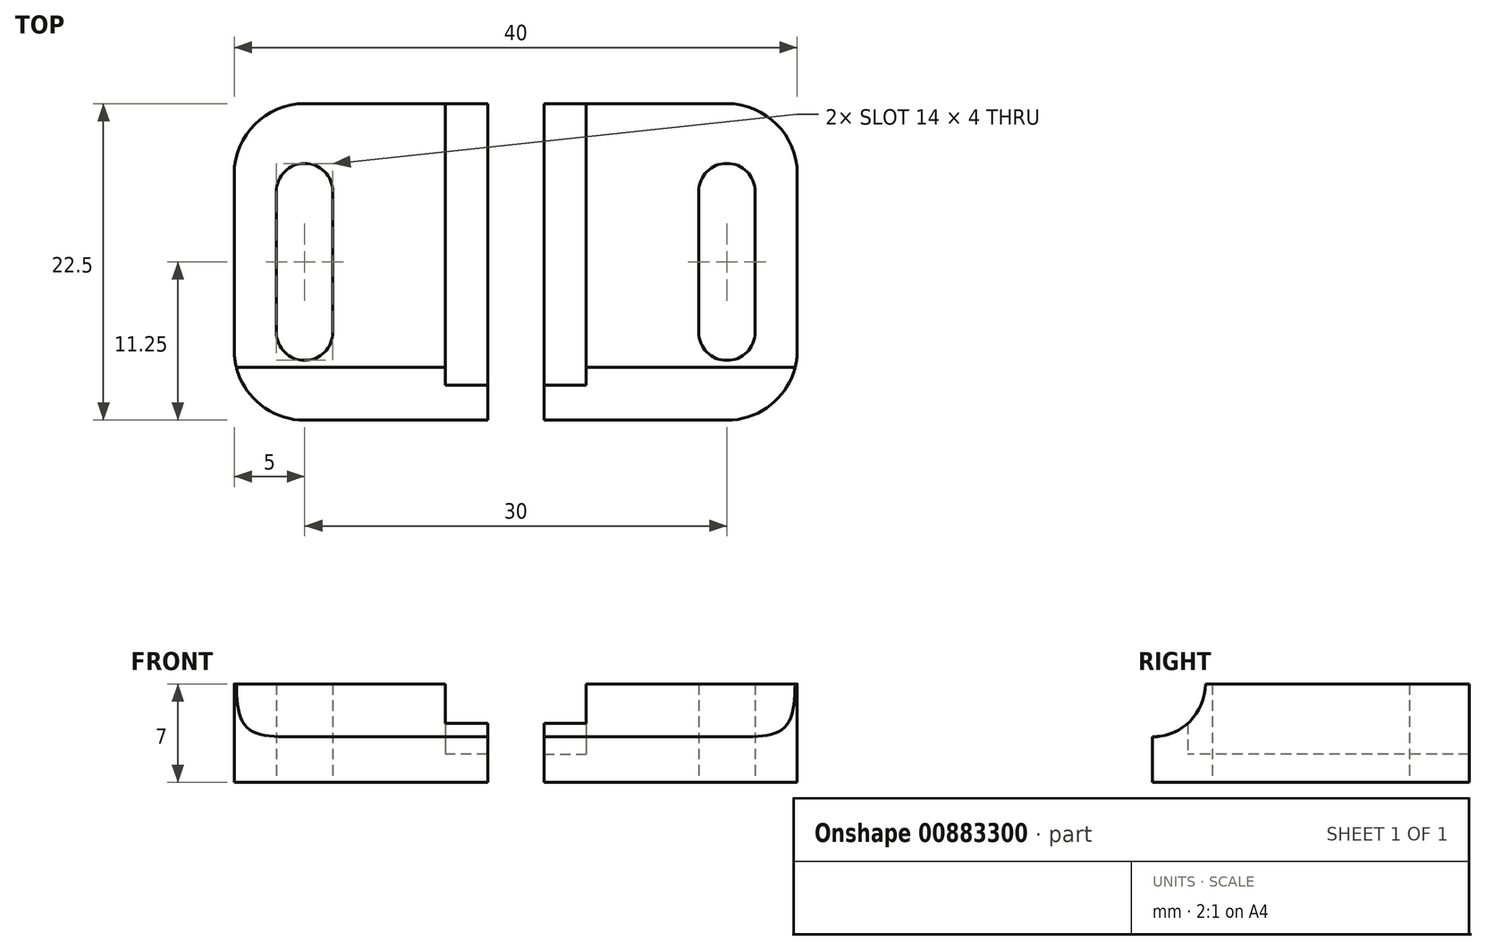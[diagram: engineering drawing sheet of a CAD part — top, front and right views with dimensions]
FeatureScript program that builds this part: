
annotation { "Feature Type Name" : "Feature", "Feature Type Description" : "" }
export const myFeature = defineFeature(function(context is Context, id is Id, definition is map)
    precondition{}
    {
        {
            var Q0;
            Q0=qCreatedBy(makeId("Top.planeOp"),FACE);
            var sketch = newSketch(context, id + "F0", { "sketchPlane" : qUnion([Q0])});
            skLineSegment(sketch, "E0", {"start": v(-2, 0) * mm, "end": v(-2, 2.5) * mm});
            skLineSegment(sketch, "E1", {"start": v(0, 2.5) * mm, "end": v(-5, 2.5) * mm});
            skLineSegment(sketch, "E2", {"start": v(-5, 2.5) * mm, "end": v(-5, 22.5) * mm});
            skLineSegment(sketch, "E3", {"start": v(-5, 22.5) * mm, "end": v(-20, 22.5) * mm});
            skLineSegment(sketch, "E4", {"start": v(-20, 22.5) * mm, "end": v(-20, 0) * mm});
            skLineSegment(sketch, "E5", {"start": v(-20, 0) * mm, "end": v(0, 0) * mm});
            skLineSegment(sketch, "E6", {"start": v(-20, 22.5) * mm, "end": v(-15, 22.5) * mm});
            skLineSegment(sketch, "E7.left", {"start": v(-13, 16.25) * mm, "end": v(-13, 6.25) * mm});
            skLineSegment(sketch, "E7.right", {"start": v(-17, 16.25) * mm, "end": v(-17, 6.25) * mm});
            skPoint(sketch, "E7.middle", {"position": v(-15, 11.25) * mm});
            skCircle(sketch, "E8", {"center": v(-15, 16.25) * mm, "radius": 2 * mm});
            skCircle(sketch, "E9", {"center": v(-15, 6.25) * mm, "radius": 2 * mm});
            skLineSegment(sketch, "E10", {"start": v(-5, 22.5) * mm, "end": v(0, 22.5) * mm});
            skLineSegment(sketch, "E11", {"start": v(-2, 22.5) * mm, "end": v(-2, 2.5) * mm});
            skSolve(sketch);
        }
        {
            var Q0;
            Q0=makeQuery(id+"F0.imprint","IMPRINT",FACE,{"disambiguationData":[TD([[makeQuery(id+"F0.imprint","IMPRINT",EDGE,{"derivedFrom":sQuery(id+"F0.wireOp",EDGE,"E0")}),1.0]])]});
            extrude(context, id + "F1", {"entities" : qUnion([Q0]), "depth" : 5 * mm, "offsetDistance" : 25 * mm});
        }
        {
            var Q0;
            Q0 = qSketchRegion(id + "F0", true);
            extrude(context, id + "F2", {"entities" : qUnion([Q0]), "operationType" : NewBodyOperationType.ADD, "depth" : -2 * mm, "offsetDistance" : 25 * mm});
        }
        {
            var Q0;
            {var subQ0=sQuery(id+"F0.wireOp",EDGE,"E0");Q0=makeQuery(id+"F2.boolean.opBoolean","MERGE",FACE,{"derivedFrom":[makeQuery(id+"F1.opExtrude","SWEPT_FACE",FACE,{"disambiguationData":[OSD([subQ0])]}),makeQuery(id+"F2.opExtrude","SWEPT_FACE",FACE,{"disambiguationData":[OSD([subQ0,sQuery(id+"F0.wireOp",EDGE,"E11")])]})]});}
            var sketch = newSketch(context, id + "F3", { "sketchPlane" : qUnion([Q0])});
            skCircle(sketch, "E12", {"center": v(0, 5) * mm, "radius": 3.75 * mm});
            skSolve(sketch);
        }
        {
            var Q0;
            Q0 = qSketchRegion(id + "F3", true);
            extrude(context, id + "F4", {"entities" : qUnion([Q0]), "operationType" : NewBodyOperationType.REMOVE, "oppositeDirection" : true, "depth" : 25 * mm, "offsetDistance" : 25 * mm});
        }
        {
            var Q0;
            {var subQ0=sQuery(id+"F0.wireOp",EDGE,"E5");var subQ1=sQuery(id+"F0.wireOp",EDGE,"E4");Q0=makeQuery(id+"F2.boolean.opBoolean","MERGE",EDGE,{"derivedFrom":[makeQuery(id+"F1.opExtrude","SWEPT_EDGE",EDGE,{"disambiguationData":[OSD([subQ1,subQ0])]}),makeQuery(id+"F2.opExtrude","SWEPT_EDGE",EDGE,{"disambiguationData":[OSD([subQ1,subQ0])]})]});}
            var Q1;
            {var subQ0=sQuery(id+"F0.wireOp",EDGE,"E4");var subQ1=sQuery(id+"F0.wireOp",EDGE,"E3");Q1=makeQuery(id+"F2.boolean.opBoolean","MERGE",EDGE,{"derivedFrom":[makeQuery(id+"F1.opExtrude","SWEPT_EDGE",EDGE,{"disambiguationData":[OSD([subQ1,subQ0])]}),makeQuery(id+"F2.opExtrude","SWEPT_EDGE",EDGE,{"disambiguationData":[OSD([subQ1,subQ0])]})]});}
            fillet(context, id + "F5", {"entities" : qUnion([Q0, Q1]), "tangentPropagation" : true, "radius" : 5 * mm, "defaultsChanged" : false, "vertexSettings" : [], "allowEdgeOverflow" : false});
        }
        {
            var Q0;
            Q0=makeQuery(id+"F1.opExtrude","SWEPT_BODY",BODY,{"disambiguationData":[OSD([sQuery(id+"F0.wireOp",EDGE,"E0"),sQuery(id+"F0.wireOp",EDGE,"E1"),sQuery(id+"F0.wireOp",EDGE,"E2"),sQuery(id+"F0.wireOp",EDGE,"E3"),sQuery(id+"F0.wireOp",EDGE,"E4"),sQuery(id+"F0.wireOp",EDGE,"E5"),sQuery(id+"F0.wireOp",EDGE,"E7.left"),sQuery(id+"F0.wireOp",EDGE,"E7.right"),sQuery(id+"F0.wireOp",EDGE,"E8"),sQuery(id+"F0.wireOp",EDGE,"E9")])]});
            var Q1;
            Q1=qCreatedBy(makeId("Right.planeOp"),FACE);
            mirror(context, id + "F6", {"entities" : qUnion([Q0]), "mirrorPlane" : qUnion([Q1])});
        }
    });
